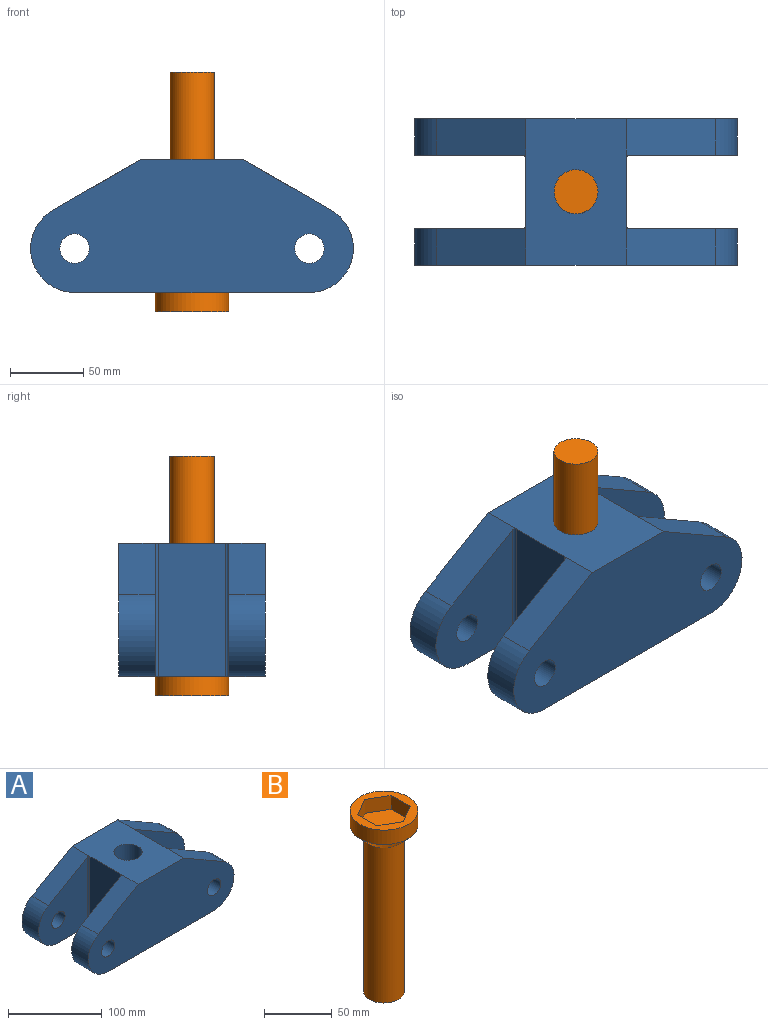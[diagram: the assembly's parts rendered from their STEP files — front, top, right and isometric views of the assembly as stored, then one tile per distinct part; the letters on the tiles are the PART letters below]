
ASSEMBLY  parts=2 mates=1
PART A: 28 faces, bbox 220x100x91 mm
  f0: plane 160x100mm, normal (0,0,-1), area 9477.8mm2, adj f1,f6,f8,f9,f10,f11,f12,f13
  f1: cylinder r=30mm len=55.98mm, axis (0,1,0), area 1963.5mm2, adj f0,f2,f8,f9
  f2: plane 60.62x35mm, normal (0.5,0,0.87), area 1751mm2, adj f1,f3,f8,f9,f27
  f3: plane 100x68.76mm, normal (0,0,1), area 6168.8mm2, adj f2,f4,f8,f10,f12,f14,f15,f19
  f4: plane 60.62x35mm, normal (-0.5,0,0.87), area 1751mm2, adj f3,f6,f8,f11,f26
  f5: cylinder r=10mm len=25mm, axis (0,1,0), area 1570.8mm2, adj f8,f11
  f6: cylinder r=30mm len=55.98mm, axis (0,1,0), area 1963.5mm2, adj f0,f4,f8,f11
  f7: cylinder r=10mm len=25mm, axis (0,1,0), area 1570.8mm2, adj f8,f9
  f8: plane 220x90.98mm, normal (0,-1,0), area 15602.7mm2, adj f0,f1,f2,f3,f4,f5,f6,f7
  f9: plane 89.83x73.62mm, normal (0,1,0), area 4492.8mm2, adj f0,f1,f2,f7,f27
  f10: plane 90.98x46mm, normal (1,0,0), area 4185.1mm2, adj f0,f3,f24,f27
  f11: plane 89.83x73.62mm, normal (0,1,0), area 4492.8mm2, adj f0,f4,f5,f6,f26
  f12: plane 90.98x46mm, normal (-1,0,0), area 4185.1mm2, adj f0,f3,f25,f26
  f13: cylinder r=30mm len=55.98mm, axis (0,-1,0), area 1963.5mm2, adj f0,f14,f19,f20
  f14: plane 60.62x35mm, normal (0.5,0,0.87), area 1751mm2, adj f3,f13,f19,f20,f24
  f15: plane 60.62x35mm, normal (-0.5,0,0.87), area 1751mm2, adj f3,f17,f19,f21,f25
  f16: cylinder r=10mm len=25mm, axis (0,-1,0), area 1570.8mm2, adj f19,f21
  f17: cylinder r=30mm len=55.98mm, axis (0,-1,0), area 1963.5mm2, adj f0,f15,f19,f21
  f18: cylinder r=10mm len=25mm, axis (0,-1,0), area 1570.8mm2, adj f19,f20
  f19: plane 220x90.98mm, normal (0,1,0), area 15602.7mm2, adj f0,f3,f13,f14,f15,f16,f17,f18
  f20: plane 89.83x73.62mm, normal (0,-1,0), area 4492.8mm2, adj f0,f13,f14,f18,f24
  f21: plane 89.83x73.62mm, normal (0,-1,0), area 4492.8mm2, adj f0,f15,f16,f17,f25
  f22: cylinder r=15mm len=80.98mm, axis (0,0,1), area 7632.3mm2, adj f3,f23
  f23: cone r=15mm half-angle=45deg, axis (0,0,-1), area 1777.2mm2, adj f0,f22
  f24: cylinder r=2mm len=90.98mm, axis (0,0,1), area 284.5mm2, adj f0,f10,f14,f20
  f25: cylinder r=2mm len=90.98mm, axis (0,0,-1), area 284.5mm2, adj f0,f12,f15,f21
  f26: cylinder r=2mm len=90.98mm, axis (0,0,-1), area 284.5mm2, adj f0,f4,f11,f12
  f27: cylinder r=2mm len=90.98mm, axis (0,0,1), area 284.5mm2, adj f0,f2,f9,f10
PART B: 12 faces, bbox 50x50x163 mm
  f0: plane 30x30mm, normal (0,0,-1), area 706.9mm2, adj f1
  f1: cylinder r=15mm len=140mm, axis (0,0,-1), area 13194.7mm2, adj f0,f2
  f2: cone r=15mm half-angle=45deg, axis (0,0,1), area 1777.2mm2, adj f1,f3
  f3: cylinder r=25mm len=50mm, axis (0,0,-1), area 2042mm2, adj f2,f4
  f4: plane 50x50mm, normal (0,0,1), area 924.3mm2, adj f3,f5,f6,f7,f8,f9,f10
  f5: plane 17.32x12.5mm, normal (0.5,0.87,0), area 250mm2, adj f4,f6,f10,f11
  f6: plane 17.32x12.5mm, normal (-0.5,0.87,0), area 250mm2, adj f4,f5,f7,f11
  f7: plane 20x12.5mm, normal (-1,0,0), area 250mm2, adj f4,f6,f8,f11
  f8: plane 17.32x12.5mm, normal (-0.5,-0.87,0), area 250mm2, adj f4,f7,f9,f11
  f9: plane 17.32x12.5mm, normal (0.5,-0.87,0), area 250mm2, adj f4,f8,f10,f11
  f10: plane 20x12.5mm, normal (1,0,0), area 250mm2, adj f4,f5,f9,f11
  f11: plane 40x34.64mm, normal (0,0,1), area 1039.2mm2, adj f5,f6,f7,f8,f9,f10
PLACE A t=(0,0,-50.49)mm
PLACE B rot(axis=(0,1,0),180deg) t=(0,0,99.51)mm
MATE cylindrical B.f1 <-> A.f22  axis (0,0,-1) through (0,0,-40.49)mm
